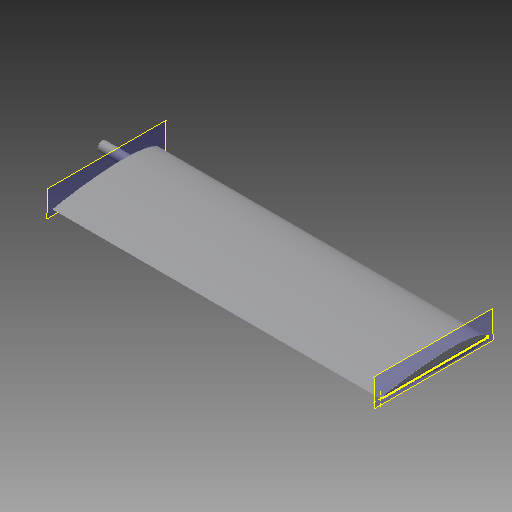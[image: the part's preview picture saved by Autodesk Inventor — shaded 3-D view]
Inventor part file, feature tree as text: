
AUTODESK INVENTOR PART (.ipt)
format: ipt  version: 2018 (Build 220112000, 112)  size: 102,400 bytes
history: native  units: in
note: dims shown in document units (in); Inventor stores cm internally (conversion verified against a paired STEP export)
features: other x3, plane x3, sketch x2
ambient origin geometry x8: Origin, YZ Plane, XZ Plane, XY Plane, X Axis, Y Axis, Z Axis, Center Point
bodies: Solid1 (feature_tree)
feature tree (8):
  other  "Generic Wing 1.ipt"
  other  "Solid1::Generic Wing 1.ipt"
  other  "TaggingFeature1"
  sketch  "Sketch1"  dims[d0=0.3937in]
  sketch  "Sketch2"
  plane  "Work Plane1"
  plane  "Work Plane2"
  plane  "Work Plane3"
